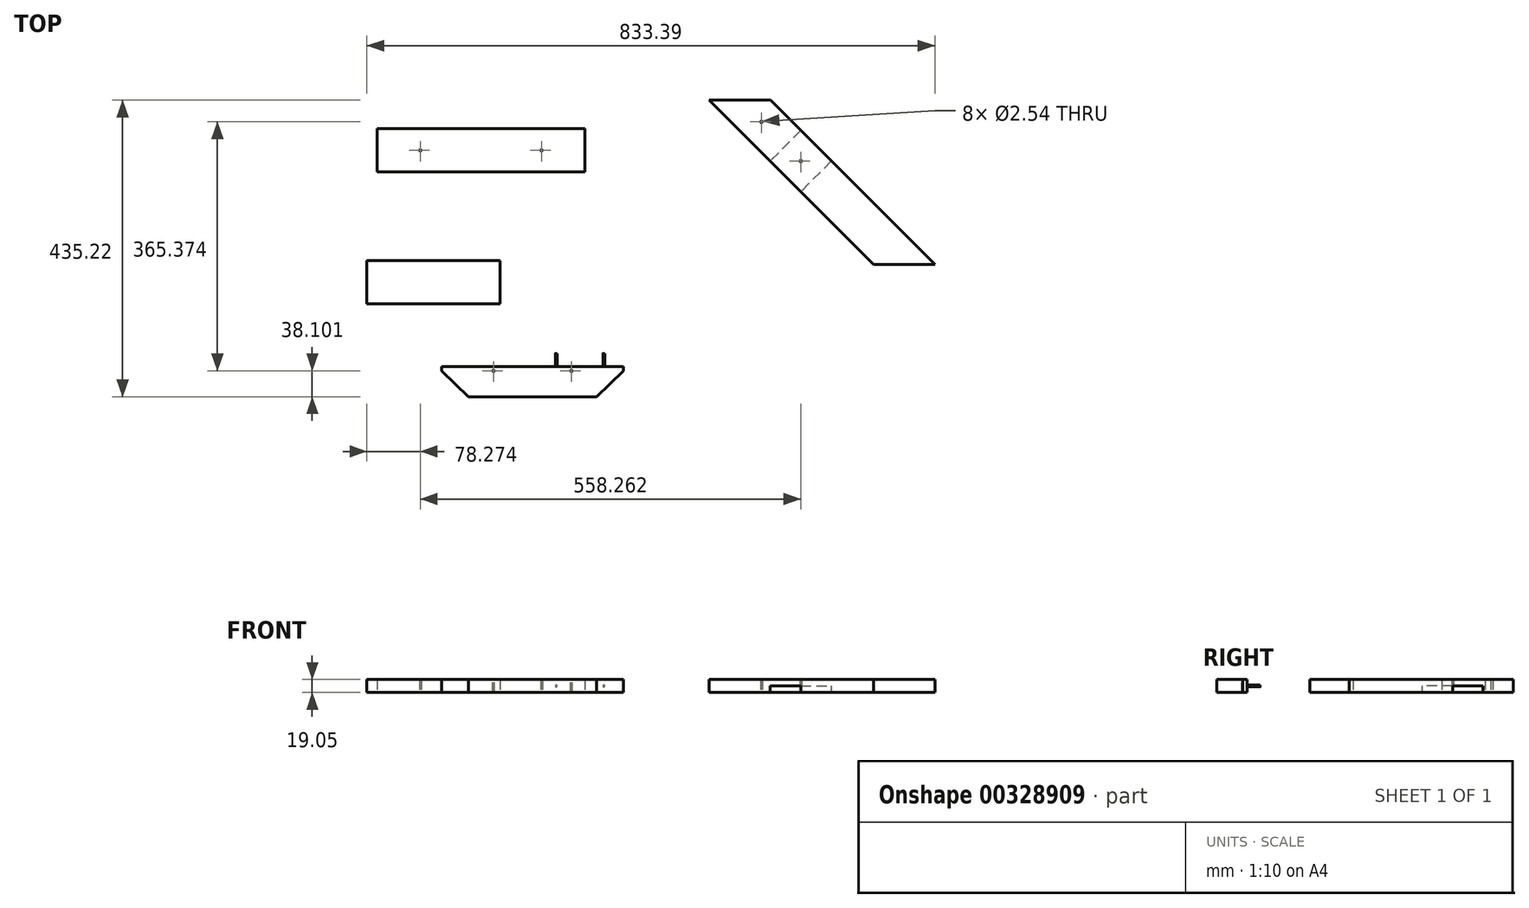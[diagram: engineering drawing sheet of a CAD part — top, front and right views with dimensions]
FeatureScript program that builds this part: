
annotation { "Feature Type Name" : "Feature", "Feature Type Description" : "" }
export const myFeature = defineFeature(function(context is Context, id is Id, definition is map)
    precondition{}
    {
        {
            var Q0;
            Q0=qCreatedBy(makeId("Top.planeOp"),FACE);
            var sketch = newSketch(context, id + "F0", { "sketchPlane" : qUnion([Q0])});
            skLineSegment(sketch, "E0", {"start": v(-338.28, 71.35) * mm, "end": v(-338.28, 7.85) * mm});
            skLineSegment(sketch, "E1", {"start": v(-338.28, 7.85) * mm, "end": v(-33.48, 7.85) * mm});
            skLineSegment(sketch, "E2", {"start": v(-33.48, 7.85) * mm, "end": v(-33.48, 71.35) * mm});
            skLineSegment(sketch, "E3", {"start": v(-33.48, 71.35) * mm, "end": v(-338.28, 71.35) * mm});
            skLineSegment(sketch, "E4", {"start": v(-33.48, 39.6) * mm, "end": v(-96.98, 39.6) * mm});
            skLineSegment(sketch, "E5", {"start": v(-33.48, 39.6) * mm, "end": v(-274.78, 39.6) * mm});
            skCircle(sketch, "E6", {"center": v(-274.78, 39.6) * mm, "radius": 1.27 * mm});
            skCircle(sketch, "E7", {"center": v(-96.98, 39.6) * mm, "radius": 1.27 * mm});
            skSolve(sketch);
        }
        {
            var Q0;
            Q0=makeQuery(id+"F0.imprint","IMPRINT",FACE,{"disambiguationData":[TD([[makeQuery(id+"F0.imprint","IMPRINT",EDGE,{"derivedFrom":sQuery(id+"F0.wireOp",EDGE,"E0")}),1.0]])]});
            extrude(context, id + "F1", {"entities" : qUnion([Q0]), "depth" : 19.05 * mm});
        }
        {
            var Q0;
            Q0=qCreatedBy(makeId("Top.planeOp"),FACE);
            var sketch = newSketch(context, id + "F2", { "sketchPlane" : qUnion([Q0])});
            skLineSegment(sketch, "E8", {"start": v(-243.57, -258.6) * mm, "end": v(-243.57, -322.1) * mm});
            skLineSegment(sketch, "E9", {"start": v(-204.16, -322.1) * mm, "end": v(-16.29, -322.1) * mm});
            skLineSegment(sketch, "E10", {"start": v(23.13, -284) * mm, "end": v(23.13, -258.6) * mm});
            skLineSegment(sketch, "E11", {"start": v(23.13, -258.6) * mm, "end": v(-243.57, -258.6) * mm});
            skLineSegment(sketch, "E12", {"start": v(-110.22, -258.6) * mm, "end": v(-110.22, -192.32) * mm});
            skPoint(sketch, "E12.endSnap0", {"position": v(-110.22, -258.6) * mm});
            skLineSegment(sketch, "E13", {"start": v(23.13, -258.6) * mm, "end": v(23.13, -181.43) * mm});
            skLineSegment(sketch, "E14", {"start": v(23.13, -181.43) * mm, "end": v(70.1, -240.3) * mm});
            skLineSegment(sketch, "E15", {"start": v(23.13, -322.1) * mm, "end": v(23.13, -284) * mm});
            skLineSegment(sketch, "E16", {"start": v(-16.29, -322.1) * mm, "end": v(23.13, -284) * mm});
            skLineSegment(sketch, "E17.MirrorCS", {"start": v(44, -418.14) * mm, "end": v(110.25, -420.39) * mm});
            skLineSegment(sketch, "E18.MirrorCS", {"start": v(-204.16, -322.1) * mm, "end": v(-243.57, -284) * mm});
            skSolve(sketch);
        }
        {
            var Q0;
            Q0=makeQuery(id+"F2.imprint","IMPRINT",FACE,{"disambiguationData":[TD([[makeQuery(id+"F2.imprint","IMPRINT",EDGE,{"derivedFrom":sQuery(id+"F2.wireOp",EDGE,"E8")}),1.0]])]});
            extrude(context, id + "F3", {"entities" : qUnion([Q0]), "depth" : 19.05 * mm});
        }
        {
            var Q0;
            Q0=qCreatedBy(makeId("Top.planeOp"),FACE);
            var sketch = newSketch(context, id + "F4", { "sketchPlane" : qUnion([Q0])});
            skLineSegment(sketch, "E19", {"start": v(242.26, -458.96) * mm, "end": v(332.06, -458.96) * mm});
            skLineSegment(sketch, "E20", {"start": v(573.36, -217.66) * mm, "end": v(483.56, -217.66) * mm});
            skLineSegment(sketch, "E21", {"start": v(483.56, -217.66) * mm, "end": v(242.26, -458.96) * mm});
            skLineSegment(sketch, "E22.0", {"start": v(573.36, -217.66) * mm, "end": v(332.06, -458.96) * mm});
            skLineSegment(sketch, "E23", {"start": v(332.06, -458.96) * mm, "end": v(242.26, -458.96) * mm});
            skLineSegment(sketch, "E24", {"start": v(497.61, -248.51) * mm, "end": v(495.81, -250.3) * mm});
            skLineSegment(sketch, "E25.MirrorCS", {"start": v(439.11, -262.1) * mm, "end": v(484.01, -307) * mm});
            skCircle(sketch, "E26", {"center": v(439.11, -307) * mm, "radius": 1.27 * mm});
            skCircle(sketch, "E27", {"center": v(496.71, -249.4) * mm, "radius": 1.27 * mm});
            skLineSegment(sketch, "E28.trimOffspring", {"start": v(438.21, -306.11) * mm, "end": v(440, -307.9) * mm});
            skLineSegment(sketch, "E29.trimOffspring", {"start": v(394.2, -307) * mm, "end": v(439.11, -351.91) * mm});
            skLineSegment(sketch, "E30.trimOffspring", {"start": v(440, -306.11) * mm, "end": v(438.21, -307.9) * mm});
            skPoint(sketch, "E31.trimOffspring.end.orphan", {"position": v(287.16, -458.96) * mm});
            skSolve(sketch);
        }
        {
            var Q0;
            Q0=qCreatedBy(makeId("Top.planeOp"),FACE);
            var sketch = newSketch(context, id + "F5", { "sketchPlane" : qUnion([Q0])});
            skLineSegment(sketch, "E32", {"start": v(149.23, 113.11) * mm, "end": v(239.04, 113.11) * mm});
            skLineSegment(sketch, "E33", {"start": v(283.49, 68.66) * mm, "end": v(238.58, 23.76) * mm});
            skLineSegment(sketch, "E34.0", {"start": v(328.39, 23.76) * mm, "end": v(283.49, -21.14) * mm});
            skLineSegment(sketch, "E35.MirrorCS", {"start": v(239.04, 113.11) * mm, "end": v(480.34, -128.19) * mm});
            skLineSegment(sketch, "E36.MirrorCS", {"start": v(149.23, 113.11) * mm, "end": v(390.53, -128.19) * mm});
            skLineSegment(sketch, "E37.MirrorCS", {"start": v(224.99, 82.26) * mm, "end": v(226.78, 80.47) * mm});
            skCircle(sketch, "E38", {"center": v(225.88, 81.36) * mm, "radius": 1.27 * mm});
            skCircle(sketch, "E39", {"center": v(283.49, 23.76) * mm, "radius": 1.27 * mm});
            skLineSegment(sketch, "E40.trimOffspring", {"start": v(390.53, -128.19) * mm, "end": v(480.34, -128.19) * mm});
            skLineSegment(sketch, "E41.trimOffspring", {"start": v(227.15, 81.36) * mm, "end": v(224.61, 81.36) * mm});
            skPoint(sketch, "E42.orphan", {"position": v(194.13, 113.11) * mm});
            skLineSegment(sketch, "E43.trimOffspring", {"start": v(284.38, 24.66) * mm, "end": v(282.59, 22.87) * mm});
            skLineSegment(sketch, "E44.trimOffspring", {"start": v(239.04, 113.11) * mm, "end": v(149.23, 113.11) * mm});
            skLineSegment(sketch, "E45.trimOffspring", {"start": v(282.59, 24.66) * mm, "end": v(284.38, 22.87) * mm});
            skPoint(sketch, "E46.orphan", {"position": v(435.43, -128.19) * mm});
            skSolve(sketch);
        }
        {
            var Q0;
            {var subQ2=sQuery(id+"F4.wireOp",EDGE,"E20");Q0=makeQuery(id+"F4.imprint","IMPRINT",FACE,{"disambiguationData":[TD([[makeQuery(id+"F4.imprint","IMPRINT",EDGE,{"derivedFrom":subQ2}),1.0]])]});}
            var Q1;
            {var subQ0=sQuery(id+"F4.wireOp",EDGE,"E25.MirrorCS");Q1=makeQuery(id+"F4.imprint","IMPRINT",FACE,{"disambiguationData":[TD([[makeQuery(id+"F4.imprint","IMPRINT",EDGE,{"derivedFrom":subQ0}),-1.0]])]});}
            var Q2;
            {var subQ0=sQuery(id+"F4.wireOp",EDGE,"E23");Q2=makeQuery(id+"F4.imprint","IMPRINT",FACE,{"disambiguationData":[TD([[makeQuery(id+"F4.imprint","IMPRINT",EDGE,{"derivedFrom":subQ0}),-1.0]])]});}
            extrude(context, id + "F6", {"entities" : qUnion([Q0, Q1, Q2]), "depth" : 19.05 * mm});
        }
        {
            var Q0;
            {var subQ0=sQuery(id+"F5.wireOp",EDGE,"E34.0");Q0=makeQuery(id+"F5.imprint","IMPRINT",FACE,{"disambiguationData":[TD([[makeQuery(id+"F5.imprint","IMPRINT",EDGE,{"derivedFrom":subQ0}),1.0]])]});}
            var Q1;
            {var subQ1=sQuery(id+"F5.wireOp",EDGE,"E33");Q1=makeQuery(id+"F5.imprint","IMPRINT",FACE,{"disambiguationData":[TD([[makeQuery(id+"F5.imprint","IMPRINT",EDGE,{"derivedFrom":subQ1}),1.0]])]});}
            var Q2;
            {var subQ1=sQuery(id+"F5.wireOp",EDGE,"E33");Q2=makeQuery(id+"F5.imprint","IMPRINT",FACE,{"disambiguationData":[TD([[makeQuery(id+"F5.imprint","IMPRINT",EDGE,{"derivedFrom":subQ1}),-1.0]])]});}
            extrude(context, id + "F7", {"entities" : qUnion([Q0, Q1, Q2]), "depth" : 19.05 * mm});
        }
        {
            var Q0;
            {var subQ0=sQuery(id+"F4.wireOp",EDGE,"E25.MirrorCS");Q0=makeQuery(id+"F4.imprint","IMPRINT",FACE,{"disambiguationData":[TD([[makeQuery(id+"F4.imprint","IMPRINT",EDGE,{"derivedFrom":subQ0}),-1.0]])]});}
            extrude(context, id + "F8", {"entities" : qUnion([Q0]), "operationType" : NewBodyOperationType.REMOVE, "depth" : 9.52 * mm});
        }
        {
            var Q0;
            {var subQ1=sQuery(id+"F5.wireOp",EDGE,"E33");Q0=makeQuery(id+"F5.imprint","IMPRINT",FACE,{"disambiguationData":[TD([[makeQuery(id+"F5.imprint","IMPRINT",EDGE,{"derivedFrom":subQ1}),1.0]])]});}
            extrude(context, id + "F9", {"entities" : qUnion([Q0]), "operationType" : NewBodyOperationType.REMOVE, "depth" : 9.52 * mm});
        }
        {
            var Q0;
            Q0=makeQuery(id+"F3.opExtrude","SWEPT_FACE",FACE,{"disambiguationData":[OSD([sQuery(id+"F2.wireOp",EDGE,"E11")])]});
            var sketch = newSketch(context, id + "F10", { "sketchPlane" : qUnion([Q0])});
            skLineSegment(sketch, "E47", {"start": v(110.22, 9.53) * mm, "end": v(113.4, 9.53) * mm});
            skCircle(sketch, "E48", {"center": v(215, 9.53) * mm, "radius": 1.27 * mm});
            skCircle(sketch, "E49", {"center": v(145.15, 9.53) * mm, "radius": 1.27 * mm});
            skPoint(sketch, "E50.endSnap0", {"position": v(110.22, 0) * mm});
            skCircle(sketch, "E51.MirrorC", {"center": v(5.45, 9.53) * mm, "radius": 1.27 * mm});
            skCircle(sketch, "E52.MirrorC", {"center": v(75.3, 9.53) * mm, "radius": 1.27 * mm});
            skSolve(sketch);
        }
        {
            var Q0;
            Q0=makeQuery(id+"F10.imprint","IMPRINT",FACE,{"disambiguationData":[TD([[makeQuery(id+"F10.imprint","IMPRINT",EDGE,{"derivedFrom":sQuery(id+"F10.wireOp",EDGE,"E51.MirrorC")}),-1.0]])]});
            var Q1;
            Q1=makeQuery(id+"F10.imprint","IMPRINT",FACE,{"disambiguationData":[TD([[makeQuery(id+"F10.imprint","IMPRINT",EDGE,{"derivedFrom":sQuery(id+"F10.wireOp",EDGE,"E52.MirrorC")}),-1.0]])]});
            var Q2;
            Q2=makeQuery(id+"F10.imprint","IMPRINT",FACE,{"disambiguationData":[TD([[makeQuery(id+"F10.imprint","IMPRINT",EDGE,{"derivedFrom":sQuery(id+"F10.wireOp",EDGE,"E49")}),1.0]])]});
            var Q3;
            Q3=makeQuery(id+"F10.imprint","IMPRINT",FACE,{"disambiguationData":[TD([[makeQuery(id+"F10.imprint","IMPRINT",EDGE,{"derivedFrom":sQuery(id+"F10.wireOp",EDGE,"E48")}),1.0]])]});
            var Q4;
            Q4=sQuery(id+"F10.wireOp",EDGE,"E48");
            var Q5;
            Q5=sQuery(id+"F10.wireOp",EDGE,"E49");
            var Q6;
            Q6=sQuery(id+"F10.wireOp",EDGE,"E52.MirrorC");
            var Q7;
            Q7=sQuery(id+"F10.wireOp",EDGE,"E51.MirrorC");
            extrude(context, id + "F11", {"entities" : qUnion([Q0, Q1, Q2, Q3]), "operationType" : NewBodyOperationType.REMOVE, "surfaceEntities" : qUnion([Q4, Q5, Q6, Q7]), "oppositeDirection" : true, "depth" : 19.05 * mm});
        }
        {
            var Q0;
            Q0=makeQuery(id+"F3.opExtrude","CAP_FACE",FACE,{"disambiguationData":[OSD([sQuery(id+"F2.wireOp",EDGE,"E8"),sQuery(id+"F2.wireOp",EDGE,"E9"),sQuery(id+"F2.wireOp",EDGE,"E10"),sQuery(id+"F2.wireOp",EDGE,"E11")])],"isStart":false});
            var sketch = newSketch(context, id + "F12", { "sketchPlane" : qUnion([Q0])});
            skLineSegment(sketch, "E53", {"start": v(-110.22, -258.6) * mm, "end": v(-110.22, -284) * mm});
            skLineSegment(sketch, "E54", {"start": v(-110.22, -284) * mm, "end": v(-53.07, -284) * mm});
            skLineSegment(sketch, "E55", {"start": v(-53.07, -284) * mm, "end": v(-167.37, -284) * mm});
            skPoint(sketch, "E55.endSnap0", {"position": v(-81.65, -284) * mm});
            skCircle(sketch, "E56", {"center": v(-167.37, -284) * mm, "radius": 1.27 * mm});
            skCircle(sketch, "E57", {"center": v(-53.07, -284) * mm, "radius": 1.27 * mm});
            skSolve(sketch);
        }
        {
            var Q0;
            Q0=makeQuery(id+"F12.imprint","IMPRINT",FACE,{"disambiguationData":[TD([[makeQuery(id+"F12.imprint","IMPRINT",EDGE,{"derivedFrom":sQuery(id+"F12.wireOp",EDGE,"E56")}),1.0]])]});
            var Q1;
            Q1=makeQuery(id+"F12.imprint","IMPRINT",FACE,{"disambiguationData":[TD([[makeQuery(id+"F12.imprint","IMPRINT",EDGE,{"derivedFrom":sQuery(id+"F12.wireOp",EDGE,"E57")}),1.0]])]});
            extrude(context, id + "F13", {"entities" : qUnion([Q0, Q1]), "operationType" : NewBodyOperationType.REMOVE, "oppositeDirection" : true, "depth" : 19.05 * mm});
        }
        {
            var Q0;
            Q0=qCreatedBy(makeId("Top.planeOp"),FACE);
            var sketch = newSketch(context, id + "F14", { "sketchPlane" : qUnion([Q0])});
            skLineSegment(sketch, "E58", {"start": v(-353.05, -122.15) * mm, "end": v(-353.05, -185.65) * mm});
            skLineSegment(sketch, "E59", {"start": v(-353.05, -185.65) * mm, "end": v(-157.47, -185.65) * mm});
            skLineSegment(sketch, "E60", {"start": v(-157.47, -185.65) * mm, "end": v(-157.47, -122.15) * mm});
            skLineSegment(sketch, "E61", {"start": v(-157.47, -122.15) * mm, "end": v(-353.05, -122.15) * mm});
            skSolve(sketch);
        }
        {
            var Q0;
            Q0 = qSketchRegion(id + "F14", true);
            extrude(context, id + "F15", {"entities" : qUnion([Q0]), "depth" : 19.05 * mm});
        }
        {
            var Q0;
            Q0=makeQuery(id+"F6.opExtrude","SWEPT_BODY",BODY,{"disambiguationData":[OSD([sQuery(id+"F4.wireOp",EDGE,"E20"),sQuery(id+"F4.wireOp",EDGE,"E21"),sQuery(id+"F4.wireOp",EDGE,"E22.0"),sQuery(id+"F4.wireOp",EDGE,"E23"),sQuery(id+"F4.wireOp",EDGE,"E26"),sQuery(id+"F4.wireOp",EDGE,"E27")])]});
            deleteBodies(context, id + "F16", {"entities" : qUnion([Q0])});
        }
        {
            var Q0;
            Q0=makeQuery(id+"F3.opExtrude","SWEPT_BODY",BODY,{"disambiguationData":[OSD([sQuery(id+"F2.wireOp",EDGE,"E8"),sQuery(id+"F2.wireOp",EDGE,"E9"),sQuery(id+"F2.wireOp",EDGE,"E10"),sQuery(id+"F2.wireOp",EDGE,"E11"),sQuery(id+"F2.wireOp",EDGE,"E16"),sQuery(id+"F2.wireOp",EDGE,"E18.MirrorCS")])]});
            transform(context, id + "F17", {"entities" : qUnion([Q0]), "transformType" : TransformType.TRANSLATION_3D, "dx" : 0 * mm, "dy" : 0 * mm, "dz" : 0 * mm, "makeCopy" : true});
        }
    });
